# Revit family: WashbasinUnit-WithShelf-Vitra-EqualSeries-64091-64100
name_source: partatom
category: Furniture Systems
revit_build: Autodesk Revit 2017 (Build: 20160225_1515(x64)
units: mm (PartAtom-declared; Revit-internal decimal feet)

## family parameters
Cut with Voids When Loaded = No
Host = Face
OmniClass Number = 23.40.00.00
OmniClass Title = Equipment and Furnishings
Part Type = Normal
Room Calculation Point = No
Round Connector Dimension = Use Diameter
Shared = Yes

## types (4) — shared parameters
BIMobject category = Bathroom compound units
Construction Type = Face Mounted
Default Elevation = 660 mm
Depth(mm) = 432 mm  [stored 1.41732 ft]
Design country = Turkey
Height(mm) = 452 mm  [stored 1.48294 ft]
IFC Classification = Furniture
Manufacturer = Vitra
Manufacturer name = Vitra
Masterformat 2014 Code = 13 42 13
Masterformat 2014 Description = Bathroom Unit Modules
NBS Referans Code = 35-75-08
NBS Referans Description = Bathroom Cabinets
Nominal height = 0.000
Nominal width = 0.000
OmniClass Code = 23-31 25 13
OmniClass Description = Bathroom Cabinets
Primary Material = Vitra-Black
Product certification = https://vitraglobal.com
Product data url = https://www.vitraglobal.com
Product family = Equal
Product group = Washbasin Unit
Secondary Material = Vitra-Black
Technical description = https://www.vitra.com.tr
UNSPSC Code = 301815
UNSPSC Description = Bathroom Cabinets
URL = https://vitraglobal.com
Uniclass 1.4 Code = L8241
Uniclass 1.4 Description = Bathroom Cabinets
Uniclass 2.0 Code = PR-35-75-08
Uniclass 2.0 Description = Bathroom Cabinets
Uniclass 2015 Code = Pr_40_20_93
Uniclass 2015 Name = Wash basins, sinks and troughs
Uniformat II Code = E20
Uniformat II Description = FURNISHINGS
Warranty Period (Year) = 2
Youtube = https://www.youtube.com

## per-type parameters (varying)
| type | Article No. (default) | Description | Model | Product SKU | Width(mm) |
| WashbasinUnit-WithShelf-Vitra-EqualSeries-100cm_64091 | 64091 | Equal Washbasin Unit, 100 cm, with Shelf | 64091 | 64091 | 1000 mm  [stored 3.28084 ft] |
| WashbasinUnit-WithShelf-Vitra-EqualSeries-130cm_64100 | 64100 | Equal Washbasin Unit, 130 cm, with Shelf | 64100 | 64100 | 1300 mm  [stored 4.26509 ft] |
| WashbasinUnit-WithShelf-Vitra-EqualSeries-130cm_64101 | 64101 | Equal Washbasin Unit, 130 cm, with Shelf | 64101 | 64101 | 1300 mm  [stored 4.26509 ft] |
| WashbasinUnit-WithShelf-Vitra-EqualSeries-100cm_64092 | 64092 | Equal Washbasin Unit, 100 cm, with Shelf | 64092 | 64092 | 1000 mm  [stored 3.28084 ft] |

note: [stored X ft] marks values corroborated as IEEE doubles in the binary element streams (Revit-internal decimal feet)

## geometry (parser evidence)
native form markers: Sweep x2
no freeform markers — native parametric forms only
